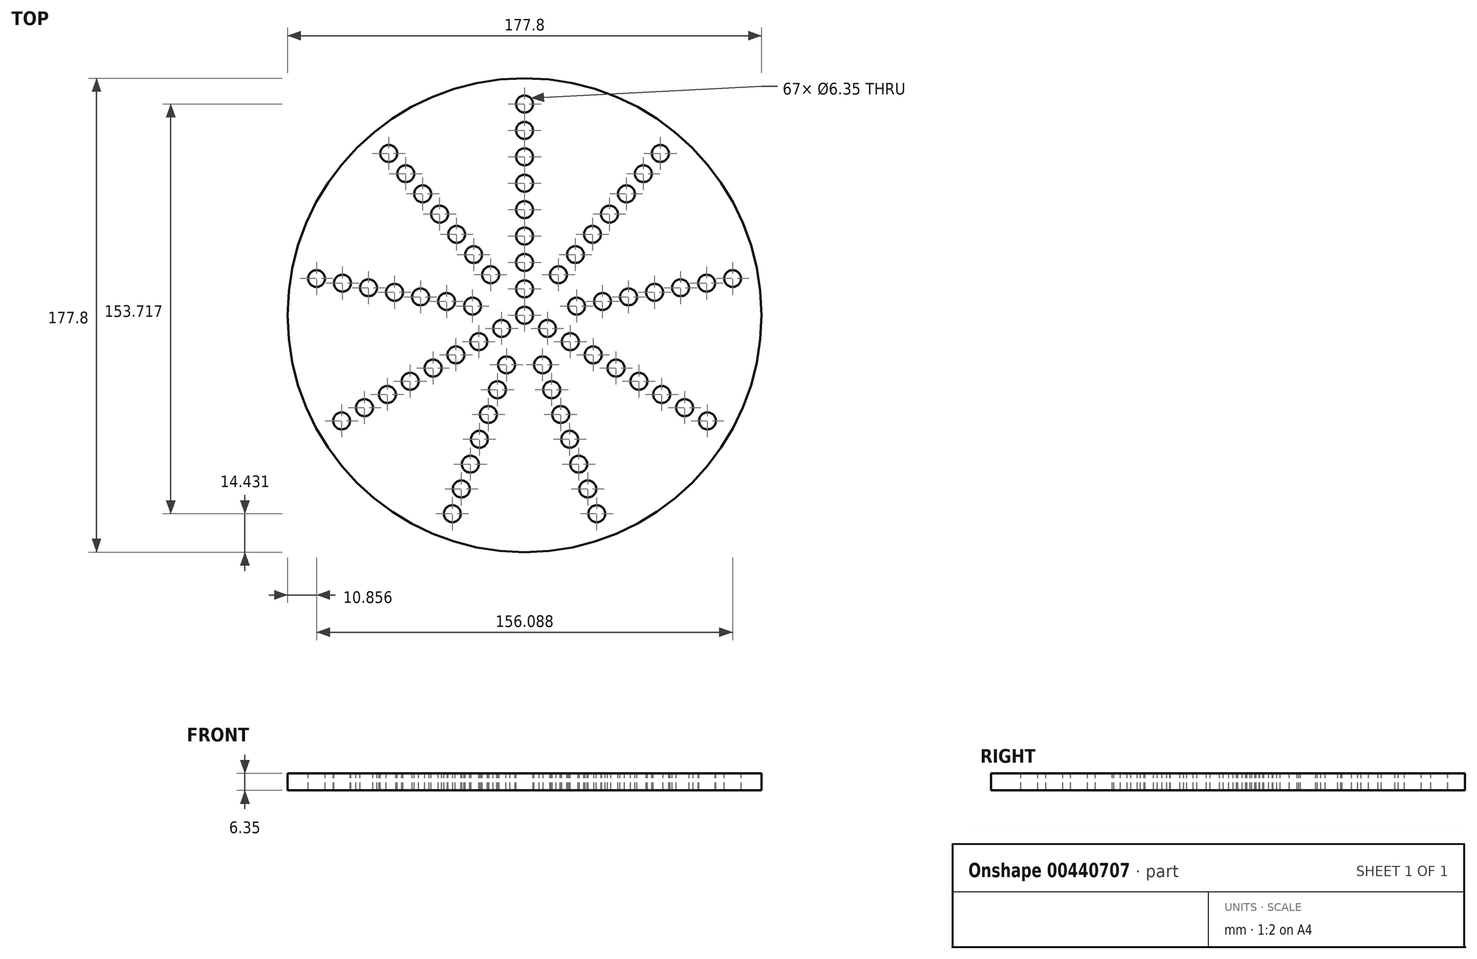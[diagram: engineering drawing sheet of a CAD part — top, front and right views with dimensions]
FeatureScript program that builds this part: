
annotation { "Feature Type Name" : "Feature", "Feature Type Description" : "" }
export const myFeature = defineFeature(function(context is Context, id is Id, definition is map)
    precondition{}
    {
        {
            var Q0;
            Q0=qCreatedBy(makeId("Top.planeOp"),FACE);
            var sketch = newSketch(context, id + "F0", { "sketchPlane" : qUnion([Q0])});
            skCircle(sketch, "E0", {"center": v(0, 0) * mm, "radius": 88.9 * mm});
            skSolve(sketch);
        }
        {
            var Q0;
            Q0 = qSketchRegion(id + "F0", true);
            extrude(context, id + "F1", {"entities" : qUnion([Q0]), "depth" : 6.35 * mm});
        }
        {
            var Q0;
            Q0=makeQuery(id+"F1.opExtrude","CAP_FACE",FACE,{"disambiguationData":[OSD([sQuery(id+"F0.wireOp",EDGE,"E0")])],"isStart":false});
            var sketch = newSketch(context, id + "F2", { "sketchPlane" : qUnion([Q0])});
            skCircle(sketch, "E1", {"center": v(0, 0) * mm, "radius": 3.18 * mm});
            skCircle(sketch, "E2", {"center": v(0, 9.9) * mm, "radius": 3.18 * mm});
            skCircle(sketch, "E3", {"center": v(0, 19.81) * mm, "radius": 3.18 * mm});
            skCircle(sketch, "E4", {"center": v(0, 29.72) * mm, "radius": 3.18 * mm});
            skCircle(sketch, "E5", {"center": v(0, 39.62) * mm, "radius": 3.18 * mm});
            skCircle(sketch, "E6", {"center": v(0, 49.53) * mm, "radius": 3.18 * mm});
            skCircle(sketch, "E7", {"center": v(0, 59.44) * mm, "radius": 3.18 * mm});
            skCircle(sketch, "E8", {"center": v(0, 69.34) * mm, "radius": 3.18 * mm});
            skCircle(sketch, "E9", {"center": v(185.83, 80.56) * mm, "radius": 3.18 * mm});
            skCircle(sketch, "E10", {"center": v(0, 79.25) * mm, "radius": 3.18 * mm});
            skCircle(sketch, "E11.1.0", {"center": v(-68.63, -39.62) * mm, "radius": 3.18 * mm});
            skCircle(sketch, "E11.1.1", {"center": v(-60.05, -34.67) * mm, "radius": 3.18 * mm});
            skCircle(sketch, "E11.1.2", {"center": v(-51.47, -29.72) * mm, "radius": 3.18 * mm});
            skCircle(sketch, "E11.1.3", {"center": v(-42.9, -24.76) * mm, "radius": 3.18 * mm});
            skCircle(sketch, "E11.1.4", {"center": v(-34.32, -19.81) * mm, "radius": 3.18 * mm});
            skCircle(sketch, "E11.1.5", {"center": v(-25.74, -14.86) * mm, "radius": 3.18 * mm});
            skCircle(sketch, "E11.1.6", {"center": v(-17.16, -9.9) * mm, "radius": 3.18 * mm});
            skCircle(sketch, "E11.1.7", {"center": v(-8.58, -4.95) * mm, "radius": 3.18 * mm});
            skCircle(sketch, "E11.2.0", {"center": v(68.63, -39.62) * mm, "radius": 3.18 * mm});
            skCircle(sketch, "E11.2.1", {"center": v(60.05, -34.67) * mm, "radius": 3.18 * mm});
            skCircle(sketch, "E11.2.2", {"center": v(51.47, -29.72) * mm, "radius": 3.18 * mm});
            skCircle(sketch, "E11.2.3", {"center": v(42.9, -24.77) * mm, "radius": 3.18 * mm});
            skCircle(sketch, "E11.2.4", {"center": v(34.32, -19.81) * mm, "radius": 3.18 * mm});
            skCircle(sketch, "E11.2.5", {"center": v(25.74, -14.86) * mm, "radius": 3.18 * mm});
            skCircle(sketch, "E11.2.6", {"center": v(17.16, -9.9) * mm, "radius": 3.18 * mm});
            skCircle(sketch, "E11.2.7", {"center": v(8.58, -4.95) * mm, "radius": 3.18 * mm});
            skCircle(sketch, "E12.1.0", {"center": v(-6.78, -18.62) * mm, "radius": 3.18 * mm});
            skCircle(sketch, "E12.1.1", {"center": v(-10.16, -27.93) * mm, "radius": 3.18 * mm});
            skCircle(sketch, "E12.1.2", {"center": v(-13.55, -37.23) * mm, "radius": 3.18 * mm});
            skCircle(sketch, "E12.1.3", {"center": v(-16.94, -46.54) * mm, "radius": 3.18 * mm});
            skCircle(sketch, "E12.1.4", {"center": v(-20.33, -55.85) * mm, "radius": 3.18 * mm});
            skCircle(sketch, "E12.1.5", {"center": v(-23.72, -65.16) * mm, "radius": 3.18 * mm});
            skCircle(sketch, "E12.1.6", {"center": v(-27.1, -74.47) * mm, "radius": 3.18 * mm});
            skCircle(sketch, "E12.1.7", {"center": v(-12.73, 15.18) * mm, "radius": 3.18 * mm});
            skCircle(sketch, "E12.1.8", {"center": v(-19.1, 22.77) * mm, "radius": 3.18 * mm});
            skCircle(sketch, "E12.1.9", {"center": v(-25.47, 30.35) * mm, "radius": 3.18 * mm});
            skCircle(sketch, "E12.1.10", {"center": v(-31.84, 37.94) * mm, "radius": 3.18 * mm});
            skCircle(sketch, "E12.1.11", {"center": v(-38.2, 45.53) * mm, "radius": 3.18 * mm});
            skCircle(sketch, "E12.1.12", {"center": v(-44.57, 53.12) * mm, "radius": 3.18 * mm});
            skCircle(sketch, "E12.1.13", {"center": v(-50.94, 60.7) * mm, "radius": 3.18 * mm});
            skCircle(sketch, "E12.1.14", {"center": v(19.51, 3.44) * mm, "radius": 3.18 * mm});
            skCircle(sketch, "E12.1.15", {"center": v(29.27, 5.16) * mm, "radius": 3.18 * mm});
            skCircle(sketch, "E12.1.16", {"center": v(39.02, 6.88) * mm, "radius": 3.18 * mm});
            skCircle(sketch, "E12.1.17", {"center": v(48.78, 8.6) * mm, "radius": 3.18 * mm});
            skCircle(sketch, "E12.1.18", {"center": v(58.53, 10.32) * mm, "radius": 3.18 * mm});
            skCircle(sketch, "E12.1.19", {"center": v(68.29, 12.04) * mm, "radius": 3.18 * mm});
            skCircle(sketch, "E12.1.20", {"center": v(78.04, 13.76) * mm, "radius": 3.18 * mm});
            skCircle(sketch, "E12.2.0", {"center": v(-19.51, 3.44) * mm, "radius": 3.18 * mm});
            skCircle(sketch, "E12.2.1", {"center": v(-29.27, 5.16) * mm, "radius": 3.18 * mm});
            skCircle(sketch, "E12.2.2", {"center": v(-39.02, 6.88) * mm, "radius": 3.18 * mm});
            skCircle(sketch, "E12.2.3", {"center": v(-48.78, 8.6) * mm, "radius": 3.18 * mm});
            skCircle(sketch, "E12.2.4", {"center": v(-58.53, 10.32) * mm, "radius": 3.18 * mm});
            skCircle(sketch, "E12.2.5", {"center": v(-68.29, 12.04) * mm, "radius": 3.18 * mm});
            skCircle(sketch, "E12.2.6", {"center": v(-78.04, 13.76) * mm, "radius": 3.18 * mm});
            skCircle(sketch, "E12.2.7", {"center": v(12.73, 15.18) * mm, "radius": 3.18 * mm});
            skCircle(sketch, "E12.2.8", {"center": v(19.1, 22.77) * mm, "radius": 3.18 * mm});
            skCircle(sketch, "E12.2.9", {"center": v(25.47, 30.35) * mm, "radius": 3.18 * mm});
            skCircle(sketch, "E12.2.10", {"center": v(31.84, 37.94) * mm, "radius": 3.18 * mm});
            skCircle(sketch, "E12.2.11", {"center": v(38.2, 45.53) * mm, "radius": 3.18 * mm});
            skCircle(sketch, "E12.2.12", {"center": v(44.57, 53.12) * mm, "radius": 3.18 * mm});
            skCircle(sketch, "E12.2.13", {"center": v(50.94, 60.7) * mm, "radius": 3.18 * mm});
            skCircle(sketch, "E12.2.14", {"center": v(6.78, -18.62) * mm, "radius": 3.18 * mm});
            skCircle(sketch, "E12.2.15", {"center": v(10.16, -27.93) * mm, "radius": 3.18 * mm});
            skCircle(sketch, "E12.2.16", {"center": v(13.55, -37.23) * mm, "radius": 3.18 * mm});
            skCircle(sketch, "E12.2.17", {"center": v(16.94, -46.54) * mm, "radius": 3.18 * mm});
            skCircle(sketch, "E12.2.18", {"center": v(20.33, -55.85) * mm, "radius": 3.18 * mm});
            skCircle(sketch, "E12.2.19", {"center": v(23.72, -65.16) * mm, "radius": 3.18 * mm});
            skCircle(sketch, "E12.2.20", {"center": v(27.1, -74.47) * mm, "radius": 3.18 * mm});
            skLineSegment(sketch, "E12.anchor1", {"start": v(0, 0) * mm, "end": v(-68.63, -39.62) * mm, "construction": true});
            skLineSegment(sketch, "E12.anchor2", {"start": v(0, 0) * mm, "end": v(50.94, 60.7) * mm, "construction": true});
            skSolve(sketch);
        }
        {
            var Q0;
            Q0 = qSketchRegion(id + "F2", true);
            extrude(context, id + "F3", {"entities" : qUnion([Q0]), "operationType" : NewBodyOperationType.REMOVE, "endBound" : BoundingType.THROUGH_ALL, "oppositeDirection" : true, "depth" : 25.4 * mm});
        }
    });
